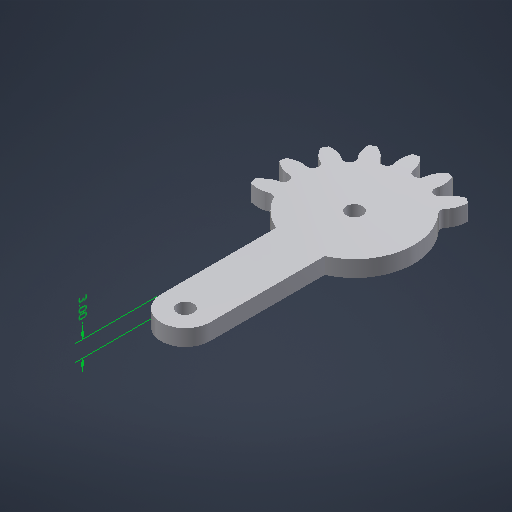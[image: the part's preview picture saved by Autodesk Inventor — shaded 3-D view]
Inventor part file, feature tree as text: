
AUTODESK INVENTOR PART (.ipt)
format: ipt  version: 2025.3 (Build 293356000, 356)  size: 493,568 bytes
history: native  units: mm
features: extrude x8, other x2, fillet x2, pattern_circular x1
ambient origin geometry x8: Origin, YZ Plane, XZ Plane, XY Plane, X Axis, Y Axis, Z Axis, Center Point
bodies: Solid1 (feature_tree)
feature tree (13):
  other  "Annotations"
  extrude  "Extrusion1"  Depth=3.0mm TaperAngle=0.0deg
  extrude  "Extrusion2"  Depth=10.0mm TaperAngle=0.0deg
  fillet  "Fillet1"  Radius=0.2mm
  pattern_circular  "Circular Pattern1"  Count=15 Angle=360.0deg
  extrude  "Extrusion3"  Depth=9.0mm
  extrude  "Extrusion4"  Depth=3.0mm
  extrude  "Extrusion5"  Depth=35.6mm TaperAngle=0.0deg
  extrude  "Extrusion6"  Depth=45.0mm TaperAngle=0.0deg
  extrude  "Extrusion7"  Depth=7.295476mm
  fillet  "Fillet5"  Radius=45.0mm
  extrude  "Extrusion10"  TaperAngle=150.0deg  [1 undecoded]
  other  "Linear Dimension 1"
note: 1 required parameter value undecoded (feature->parameter linkage not recoverable at this tier; creation-order binding heuristic only, values carry confidence <= 0.55)
